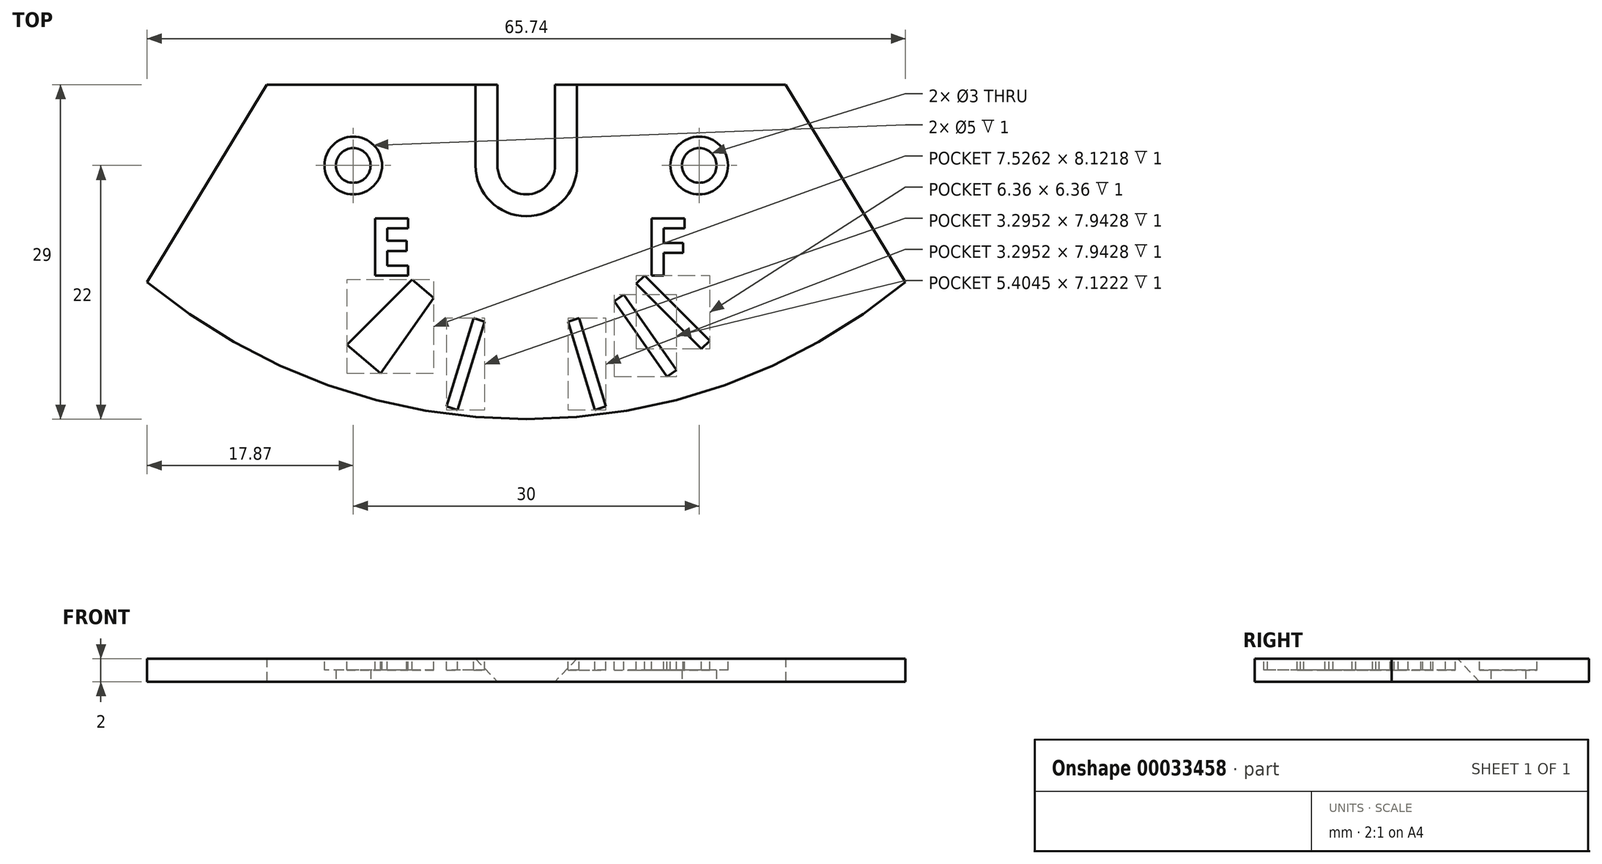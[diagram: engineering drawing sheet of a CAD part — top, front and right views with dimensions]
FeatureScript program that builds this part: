
annotation { "Feature Type Name" : "Feature", "Feature Type Description" : "" }
export const myFeature = defineFeature(function(context is Context, id is Id, definition is map)
    precondition{}
    {
        {
            var Q0;
            Q0=qCreatedBy(makeId("Top.planeOp"),FACE);
            var sketch = newSketch(context, id + "F0", { "sketchPlane" : qUnion([Q0])});
            skLineSegment(sketch, "E0", {"start": v(-2.5, 0) * mm, "end": v(2.5, 0) * mm, "construction": true});
            skArc(sketch, "E1", {"start": v(-2.5, 0) * mm, "mid": v(0, -2.5) * mm, "end": v(2.5, 0) * mm});
            skLineSegment(sketch, "E2", {"start": v(-15, 0) * mm, "end": v(15, 0) * mm, "construction": true});
            skLineSegment(sketch, "E3", {"start": v(2.5, 0) * mm, "end": v(2.5, 7) * mm});
            skLineSegment(sketch, "E4.MirrorCS", {"start": v(-2.5, 7) * mm, "end": v(-2.5, 0) * mm});
            skLineSegment(sketch, "E5", {"start": v(2.5, 7) * mm, "end": v(22.5, 7) * mm});
            skLineSegment(sketch, "E6.MirrorCS", {"start": v(-2.5, 7) * mm, "end": v(-22.5, 7) * mm});
            skCircle(sketch, "E7", {"center": v(-15, 0) * mm, "radius": 1.5 * mm});
            skCircle(sketch, "E8", {"center": v(15, 0) * mm, "radius": 1.5 * mm});
            skLineSegment(sketch, "E9", {"start": v(-22.5, 7) * mm, "end": v(-32.87, -10.1) * mm});
            skLineSegment(sketch, "E10.MirrorCS", {"start": v(22.5, 7) * mm, "end": v(32.87, -10.1) * mm});
            skLineSegment(sketch, "E11", {"start": v(0, 0) * mm, "end": v(0, -22) * mm, "construction": true});
            skArc(sketch, "E12", {"start": v(-32.87, -10.1) * mm, "mid": v(0, -22) * mm, "end": v(32.87, -10.1) * mm});
            skPoint(sketch, "E13", {"position": v(-2.5, 7) * mm});
            skSolve(sketch);
        }
        {
            var Q0;
            Q0=qSketchRegion(id+"F0",true);
            extrude(context, id + "F1", {"entities" : qUnion([Q0]), "depth" : 2 * mm});
        }
        {
            var Q0;
            Q0=makeQuery(id+"F1.opExtrude","CAP_FACE",FACE,{"disambiguationData":[OSD([sQuery(id+"F0.wireOp",EDGE,"E1"),sQuery(id+"F0.wireOp",EDGE,"E3"),sQuery(id+"F0.wireOp",EDGE,"E4.MirrorCS"),sQuery(id+"F0.wireOp",EDGE,"E5"),sQuery(id+"F0.wireOp",EDGE,"E6.MirrorCS"),sQuery(id+"F0.wireOp",EDGE,"E7"),sQuery(id+"F0.wireOp",EDGE,"E8"),sQuery(id+"F0.wireOp",EDGE,"E9"),sQuery(id+"F0.wireOp",EDGE,"E10.MirrorCS"),sQuery(id+"F0.wireOp",EDGE,"4456dc0f-3e05-4dbb-bb65-2e05c7785b1b")])],"isStart":false});
            var sketch = newSketch(context, id + "F2", { "sketchPlane" : qUnion([Q0])});
            skLineSegment(sketch, "E14", {"start": v(0, 0) * mm, "end": v(0, -22) * mm, "construction": true});
            skLineSegment(sketch, "E15", {"start": v(0, 0) * mm, "end": v(0, 22) * mm, "construction": true});
            skCircle(sketch, "E16", {"center": v(0, 0) * mm, "radius": 22 * mm, "construction": true});
            skLineSegment(sketch, "E17", {"start": v(0, 0) * mm, "end": v(-15.56, -15.56) * mm, "construction": true});
            skLineSegment(sketch, "E18", {"start": v(0, 0) * mm, "end": v(-12.62, -18.02) * mm, "construction": true});
            skLineSegment(sketch, "E19", {"start": v(0, 0) * mm, "end": v(-6.43, -21.04) * mm, "construction": true});
            skLineSegment(sketch, "E20", {"start": v(-9.9, -9.9) * mm, "end": v(-15.56, -15.56) * mm});
            skLineSegment(sketch, "E21", {"start": v(-15.56, -15.56) * mm, "end": v(-12.62, -18.02) * mm});
            skLineSegment(sketch, "E22", {"start": v(-9.9, -9.9) * mm, "end": v(-8.03, -11.47) * mm});
            skLineSegment(sketch, "E23", {"start": v(-8.03, -11.47) * mm, "end": v(-12.62, -18.02) * mm});
            skLineSegment(sketch, "E24", {"start": v(-4.57, -13.24) * mm, "end": v(-3.62, -13.53) * mm});
            skLineSegment(sketch, "E25", {"start": v(-6.43, -21.04) * mm, "end": v(-4.1, -13.39) * mm, "construction": true});
            skLineSegment(sketch, "E26", {"start": v(-6.91, -20.9) * mm, "end": v(-5.95, -21.18) * mm});
            skLineSegment(sketch, "E27", {"start": v(-4.57, -13.24) * mm, "end": v(-6.91, -20.9) * mm});
            skLineSegment(sketch, "E28", {"start": v(-3.62, -13.53) * mm, "end": v(-5.95, -21.18) * mm});
            skLineSegment(sketch, "E29.MirrorCS", {"start": v(8.03, -11.47) * mm, "end": v(12.62, -18.02) * mm, "construction": true});
            skLineSegment(sketch, "E30.MirrorCS", {"start": v(9.9, -9.9) * mm, "end": v(15.56, -15.56) * mm});
            skLineSegment(sketch, "E31.MirrorCS", {"start": v(4.57, -13.24) * mm, "end": v(3.62, -13.53) * mm});
            skLineSegment(sketch, "E32.MirrorCS", {"start": v(3.62, -13.53) * mm, "end": v(5.95, -21.18) * mm});
            skLineSegment(sketch, "E33.MirrorCS", {"start": v(4.57, -13.24) * mm, "end": v(6.91, -20.9) * mm});
            skLineSegment(sketch, "E34.MirrorCS", {"start": v(6.91, -20.9) * mm, "end": v(5.95, -21.18) * mm});
            skLineSegment(sketch, "E35", {"start": v(7.62, -11.75) * mm, "end": v(8.44, -11.18) * mm});
            skLineSegment(sketch, "E36", {"start": v(7.62, -11.75) * mm, "end": v(12.2, -18.3) * mm});
            skLineSegment(sketch, "E37", {"start": v(12.2, -18.3) * mm, "end": v(13.02, -17.73) * mm});
            skLineSegment(sketch, "E38", {"start": v(13.02, -17.73) * mm, "end": v(8.44, -11.18) * mm});
            skLineSegment(sketch, "E39", {"start": v(9.55, -10.25) * mm, "end": v(10.25, -9.55) * mm});
            skLineSegment(sketch, "E40", {"start": v(9.55, -10.25) * mm, "end": v(15.2, -15.9) * mm});
            skLineSegment(sketch, "E41", {"start": v(15.2, -15.9) * mm, "end": v(15.9, -15.2) * mm});
            skLineSegment(sketch, "E42", {"start": v(15.9, -15.2) * mm, "end": v(10.25, -9.55) * mm});
            skText(sketch, "E43", { "text": "E", "fontName": "OpenSans-Bold.ttf"});
            skText(sketch, "E44", { "text": "F", "fontName": "OpenSans-Bold.ttf"});
            skLineSegment(sketch, "E45", {"start": v(-11.99, -4.55) * mm, "end": v(11.99, -4.55) * mm, "construction": true});
            skPoint(sketch, "E46", {"position": v(0, -4.55) * mm});
            skCircle(sketch, "E47.0", {"center": v(-15, 0) * mm, "radius": 1.5 * mm});
            skCircle(sketch, "E48", {"center": v(-15, 0) * mm, "radius": 2.5 * mm});
            skCircle(sketch, "E49.MirrorC", {"center": v(15, 0) * mm, "radius": 2.5 * mm});
            const initialGuessF2  = {"E43": [-0.01373, -0.00955, 1, 0, 0.005], "E44": [0.01025, -0.00955, 1, 0, 0.005]};
            skSetInitialGuess(sketch, initialGuessF2);
            skSolve(sketch);
        }
        {
            var Q0;
            Q0=qSketchRegion(id+"F2",true);
            extrude(context, id + "F3", {"entities" : qUnion([Q0]), "operationType" : NewBodyOperationType.REMOVE, "oppositeDirection" : true, "depth" : 1 * mm});
        }
        {
            var Q0;
            Q0=makeQuery(id+"F0.imprint","IMPRINT",FACE,{"disambiguationData":[TD([[makeQuery(id+"F0.imprint","IMPRINT",EDGE,{"derivedFrom":sQuery(id+"F0.wireOp",EDGE,"E1")}),-1.0]])]});
            var sketch = newSketch(context, id + "F4", { "sketchPlane" : qUnion([Q0])});
            skLineSegment(sketch, "E50.0", {"start": v(-2.5, 7) * mm, "end": v(-2.5, 0) * mm});
            skArc(sketch, "E51.0", {"start": v(-2.5, 0) * mm, "mid": v(0, -2.5) * mm, "end": v(2.5, 0) * mm});
            skLineSegment(sketch, "E52.0", {"start": v(2.5, 0) * mm, "end": v(2.5, 7) * mm});
            skLineSegment(sketch, "E53", {"start": v(-2.5, 7) * mm, "end": v(2.5, 7) * mm});
            skSolve(sketch);
        }
        {
            var Q0;
            Q0=makeQuery(id+"F1.opExtrude","CAP_FACE",FACE,{"disambiguationData":[OSD([sQuery(id+"F0.wireOp",EDGE,"E1"),sQuery(id+"F0.wireOp",EDGE,"E3"),sQuery(id+"F0.wireOp",EDGE,"E4.MirrorCS"),sQuery(id+"F0.wireOp",EDGE,"E5"),sQuery(id+"F0.wireOp",EDGE,"E6.MirrorCS"),sQuery(id+"F0.wireOp",EDGE,"E7"),sQuery(id+"F0.wireOp",EDGE,"E8"),sQuery(id+"F0.wireOp",EDGE,"E9"),sQuery(id+"F0.wireOp",EDGE,"E10.MirrorCS"),sQuery(id+"F0.wireOp",EDGE,"4456dc0f-3e05-4dbb-bb65-2e05c7785b1b")])],"isStart":false});
            cPlane(context, id + "F5", {"entities" : qUnion([Q0]), "cplaneType" : CPlaneType.OFFSET, "offset" : .1 * mm, "width" : 150 * mm, "height" : 150 * mm});
        }
        {
            var Q0;
            Q0=qCreatedBy(id+"F5.planeOp",FACE);
            var sketch = newSketch(context, id + "F6", { "sketchPlane" : qUnion([Q0])});
            skLineSegment(sketch, "E54.0", {"start": v(-4.5, 0) * mm, "end": v(-4.5, 7) * mm});
            skArc(sketch, "E54.1", {"start": v(-4.5, 0) * mm, "mid": v(0, -4.5) * mm, "end": v(4.5, 0) * mm});
            skLineSegment(sketch, "E54.2", {"start": v(4.5, 0) * mm, "end": v(4.5, 7) * mm});
            skLineSegment(sketch, "E54.3", {"start": v(-4.5, 7) * mm, "end": v(4.5, 7) * mm});
            skLineSegment(sketch, "E55.0", {"start": v(-2.5, 7) * mm, "end": v(-22.5, 7) * mm, "construction": true});
            skSolve(sketch);
        }
        {
            var Q1;
            Q1=makeQuery(id+"F6.imprint","IMPRINT",FACE,{"disambiguationData":[TD([[makeQuery(id+"F6.imprint","IMPRINT",EDGE,{"derivedFrom":sQuery(id+"F6.wireOp",EDGE,"E54.0")}),-1.0]])]});
            var Q2;
            Q2=makeQuery(id+"F4.imprint","IMPRINT",FACE,{"disambiguationData":[TD([[makeQuery(id+"F4.imprint","IMPRINT",EDGE,{"derivedFrom":sQuery(id+"F4.wireOp",EDGE,"E50.0")}),1.0]])]});
            loft(context, id + "F7", {"operationType" : NewBodyOperationType.REMOVE, "sheetProfilesArray" : [{ "sheetProfileEntities" : qUnion([Q1]) }, { "sheetProfileEntities" : qUnion([Q2]) }]});
        }
    });
